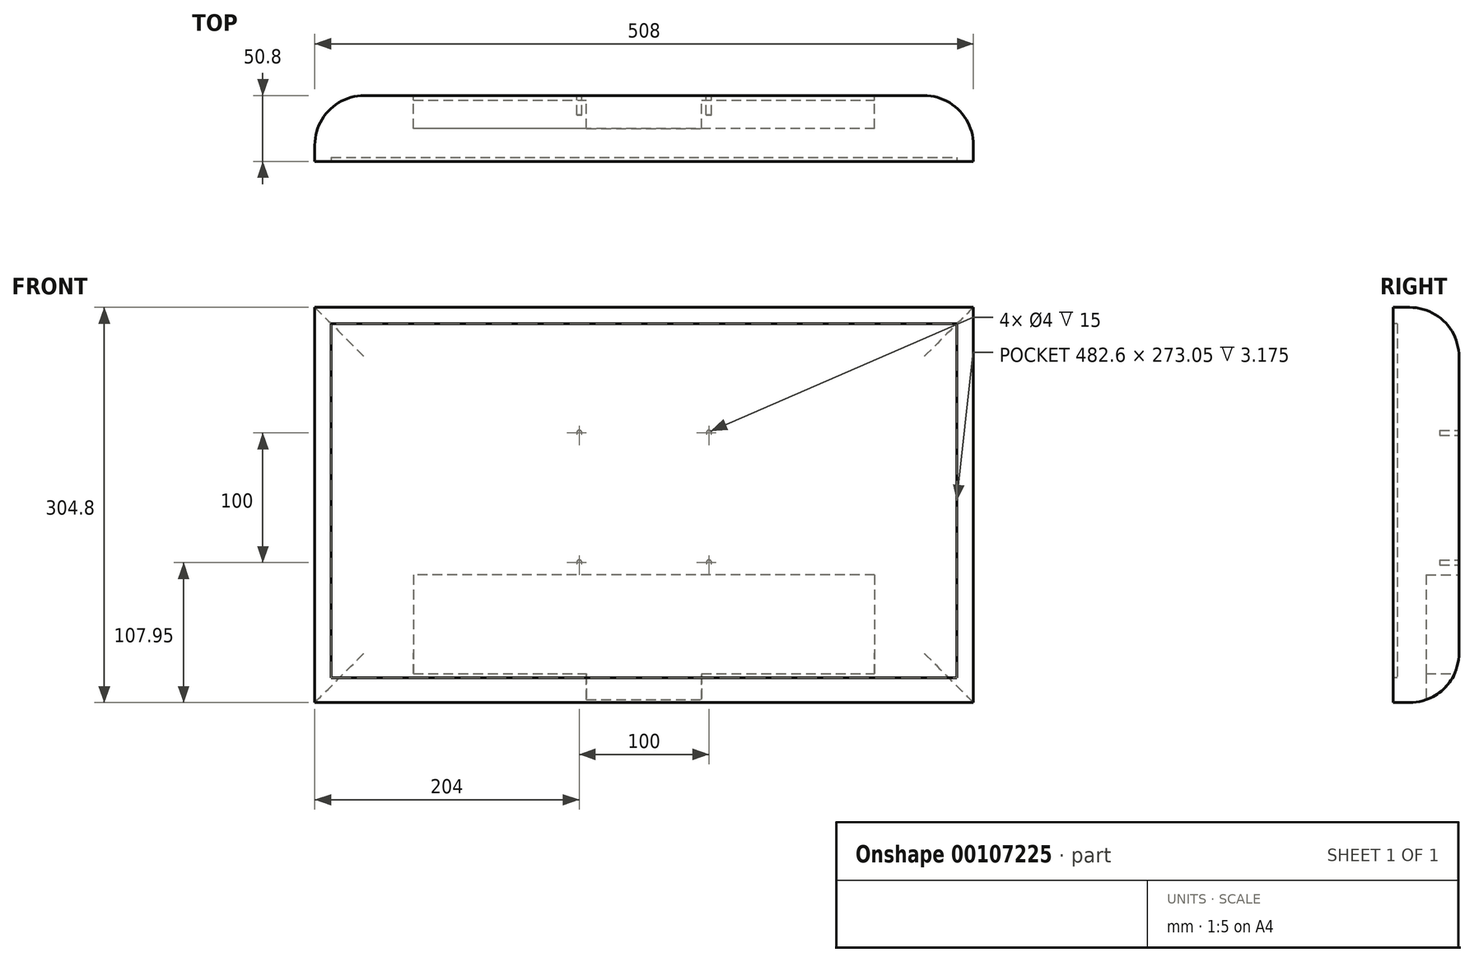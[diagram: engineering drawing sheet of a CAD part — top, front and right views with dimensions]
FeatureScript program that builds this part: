
annotation { "Feature Type Name" : "Feature", "Feature Type Description" : "" }
export const myFeature = defineFeature(function(context is Context, id is Id, definition is map)
    precondition{}
    {
        {
            var Q0;
            Q0=qCreatedBy(makeId("Front.planeOp"),FACE);
            var sketch = newSketch(context, id + "F0", { "sketchPlane" : qUnion([Q0])});
            skLineSegment(sketch, "E0.bottom", {"start": v(-254, 0) * mm, "end": v(254, 0) * mm});
            skLineSegment(sketch, "E0.top", {"start": v(-254, 304.8) * mm, "end": v(254, 304.8) * mm});
            skLineSegment(sketch, "E0.left", {"start": v(-254, 0) * mm, "end": v(-254, 304.8) * mm});
            skLineSegment(sketch, "E0.right", {"start": v(254, 0) * mm, "end": v(254, 304.8) * mm});
            skSolve(sketch);
        }
        {
            var Q0;
            Q0 = qSketchRegion(id + "F0", true);
            extrude(context, id + "F1", {"entities" : qUnion([Q0]), "depth" : 50.8 * mm});
        }
        {
            var Q0;
            Q0=makeQuery(id+"F1.opExtrude","CAP_FACE",FACE,{"disambiguationData":[OSD([sQuery(id+"F0.wireOp",EDGE,"E0.bottom"),sQuery(id+"F0.wireOp",EDGE,"E0.top"),sQuery(id+"F0.wireOp",EDGE,"E0.left"),sQuery(id+"F0.wireOp",EDGE,"E0.right")])],"isStart":false});
            var sketch = newSketch(context, id + "F2", { "sketchPlane" : qUnion([Q0])});
            skLineSegment(sketch, "E1.bottom", {"start": v(-241.3, 292.1) * mm, "end": v(241.3, 292.1) * mm});
            skLineSegment(sketch, "E1.top", {"start": v(-241.3, 19.05) * mm, "end": v(241.3, 19.05) * mm});
            skLineSegment(sketch, "E1.left", {"start": v(-241.3, 292.1) * mm, "end": v(-241.3, 19.05) * mm});
            skLineSegment(sketch, "E1.right", {"start": v(241.3, 292.1) * mm, "end": v(241.3, 19.05) * mm});
            skSolve(sketch);
        }
        {
            var Q0;
            Q0 = qSketchRegion(id + "F2", true);
            extrude(context, id + "F3", {"entities" : qUnion([Q0]), "operationType" : NewBodyOperationType.REMOVE, "oppositeDirection" : true, "depth" : 3.17 * mm});
        }
        {
            var Q0;
            Q0=makeQuery(id+"F1.opExtrude","CAP_FACE",FACE,{"disambiguationData":[OSD([sQuery(id+"F0.wireOp",EDGE,"E0.bottom"),sQuery(id+"F0.wireOp",EDGE,"E0.top"),sQuery(id+"F0.wireOp",EDGE,"E0.left"),sQuery(id+"F0.wireOp",EDGE,"E0.right")])],"isStart":true});
            var sketch = newSketch(context, id + "F4", { "sketchPlane" : qUnion([Q0])});
            skLineSegment(sketch, "E2.bottom", {"start": v(-50, 107.95) * mm, "end": v(50, 107.95) * mm, "construction": true});
            skLineSegment(sketch, "E2.top", {"start": v(-50, 207.95) * mm, "end": v(50, 207.95) * mm, "construction": true});
            skLineSegment(sketch, "E2.left", {"start": v(-50, 107.95) * mm, "end": v(-50, 207.95) * mm, "construction": true});
            skLineSegment(sketch, "E2.right", {"start": v(50, 107.95) * mm, "end": v(50, 207.95) * mm, "construction": true});
            skLineSegment(sketch, "E3", {"start": v(0, 107.95) * mm, "end": v(0, 0) * mm, "construction": true});
            skCircle(sketch, "E4", {"center": v(-50, 207.95) * mm, "radius": 2 * mm});
            skCircle(sketch, "E5", {"center": v(50, 207.95) * mm, "radius": 2 * mm});
            skCircle(sketch, "E6", {"center": v(-50, 107.95) * mm, "radius": 2 * mm});
            skCircle(sketch, "E7", {"center": v(50, 107.95) * mm, "radius": 2 * mm});
            skSolve(sketch);
        }
        {
            var Q0;
            Q0 = qSketchRegion(id + "F4", true);
            extrude(context, id + "F5", {"entities" : qUnion([Q0]), "operationType" : NewBodyOperationType.REMOVE, "oppositeDirection" : true, "depth" : 15 * mm});
        }
        {
            var Q0;
            Q0=makeQuery(id+"F1.opExtrude","CAP_FACE",FACE,{"disambiguationData":[OSD([sQuery(id+"F0.wireOp",EDGE,"E0.bottom"),sQuery(id+"F0.wireOp",EDGE,"E0.top"),sQuery(id+"F0.wireOp",EDGE,"E0.left"),sQuery(id+"F0.wireOp",EDGE,"E0.right")])],"isStart":true});
            var sketch = newSketch(context, id + "F6", { "sketchPlane" : qUnion([Q0])});
            skLineSegment(sketch, "E8.bottom", {"start": v(-177.8, 98.42) * mm, "end": v(177.8, 98.43) * mm});
            skLineSegment(sketch, "E8.top", {"start": v(-177.8, 22.22) * mm, "end": v(177.8, 22.23) * mm});
            skLineSegment(sketch, "E8.left", {"start": v(-177.8, 98.42) * mm, "end": v(-177.8, 22.22) * mm});
            skLineSegment(sketch, "E8.right", {"start": v(177.8, 98.42) * mm, "end": v(177.8, 22.22) * mm});
            skLineSegment(sketch, "E9", {"start": v(0, 0) * mm, "end": v(0, 22.23) * mm, "construction": true});
            skLineSegment(sketch, "E10.bottom", {"start": v(-44.45, 22.22) * mm, "end": v(44.45, 22.23) * mm});
            skLineSegment(sketch, "E10.top", {"start": v(-44.45, 0) * mm, "end": v(44.45, 0) * mm});
            skLineSegment(sketch, "E10.left", {"start": v(-44.45, 22.23) * mm, "end": v(-44.45, 0) * mm});
            skLineSegment(sketch, "E10.right", {"start": v(44.45, 22.23) * mm, "end": v(44.45, 0) * mm});
            skSolve(sketch);
        }
        {
            var Q0;
            Q0 = qSketchRegion(id + "F6", true);
            extrude(context, id + "F7", {"entities" : qUnion([Q0]), "operationType" : NewBodyOperationType.REMOVE, "oppositeDirection" : true, "depth" : 25.4 * mm});
        }
        {
            var Q0;
            {var subQ0=sQuery(id+"F0.wireOp",EDGE,"E0.bottom");var subQ1=sQuery(id+"F0.wireOp",EDGE,"E0.right");Q0=makeQuery(id+"F7.boolean.opBoolean","SPLIT",EDGE,{"disambiguationData":[TD([makeQuery(id+"F1.opExtrude","SWEPT_FACE",FACE,{"disambiguationData":[OSD([subQ1])]})])],"derivedFrom":makeQuery(id+"F1.opExtrude","CAP_EDGE",EDGE,{"disambiguationData":[OSD([subQ0])],"isStart":true})});}
            var Q1;
            Q1=makeQuery(id+"F1.opExtrude","CAP_EDGE",EDGE,{"disambiguationData":[OSD([sQuery(id+"F0.wireOp",EDGE,"E0.right")])],"isStart":true});
            var Q2;
            Q2=makeQuery(id+"F1.opExtrude","CAP_EDGE",EDGE,{"disambiguationData":[OSD([sQuery(id+"F0.wireOp",EDGE,"E0.top")])],"isStart":true});
            var Q3;
            Q3=makeQuery(id+"F1.opExtrude","CAP_EDGE",EDGE,{"disambiguationData":[OSD([sQuery(id+"F0.wireOp",EDGE,"E0.left")])],"isStart":true});
            var Q4;
            {var subQ0=sQuery(id+"F0.wireOp",EDGE,"E0.bottom");var subQ1=sQuery(id+"F0.wireOp",EDGE,"E0.left");Q4=makeQuery(id+"F7.boolean.opBoolean","SPLIT",EDGE,{"disambiguationData":[TD([makeQuery(id+"F1.opExtrude","SWEPT_FACE",FACE,{"disambiguationData":[OSD([subQ1])]})])],"derivedFrom":makeQuery(id+"F1.opExtrude","CAP_EDGE",EDGE,{"disambiguationData":[OSD([subQ0])],"isStart":true})});}
            fillet(context, id + "F8", {"entities" : qUnion([Q0, Q1, Q2, Q3, Q4]), "radius" : 38.1 * mm, "tangentPropagation" : true, "allowEdgeOverflow" : false});
        }
    });
